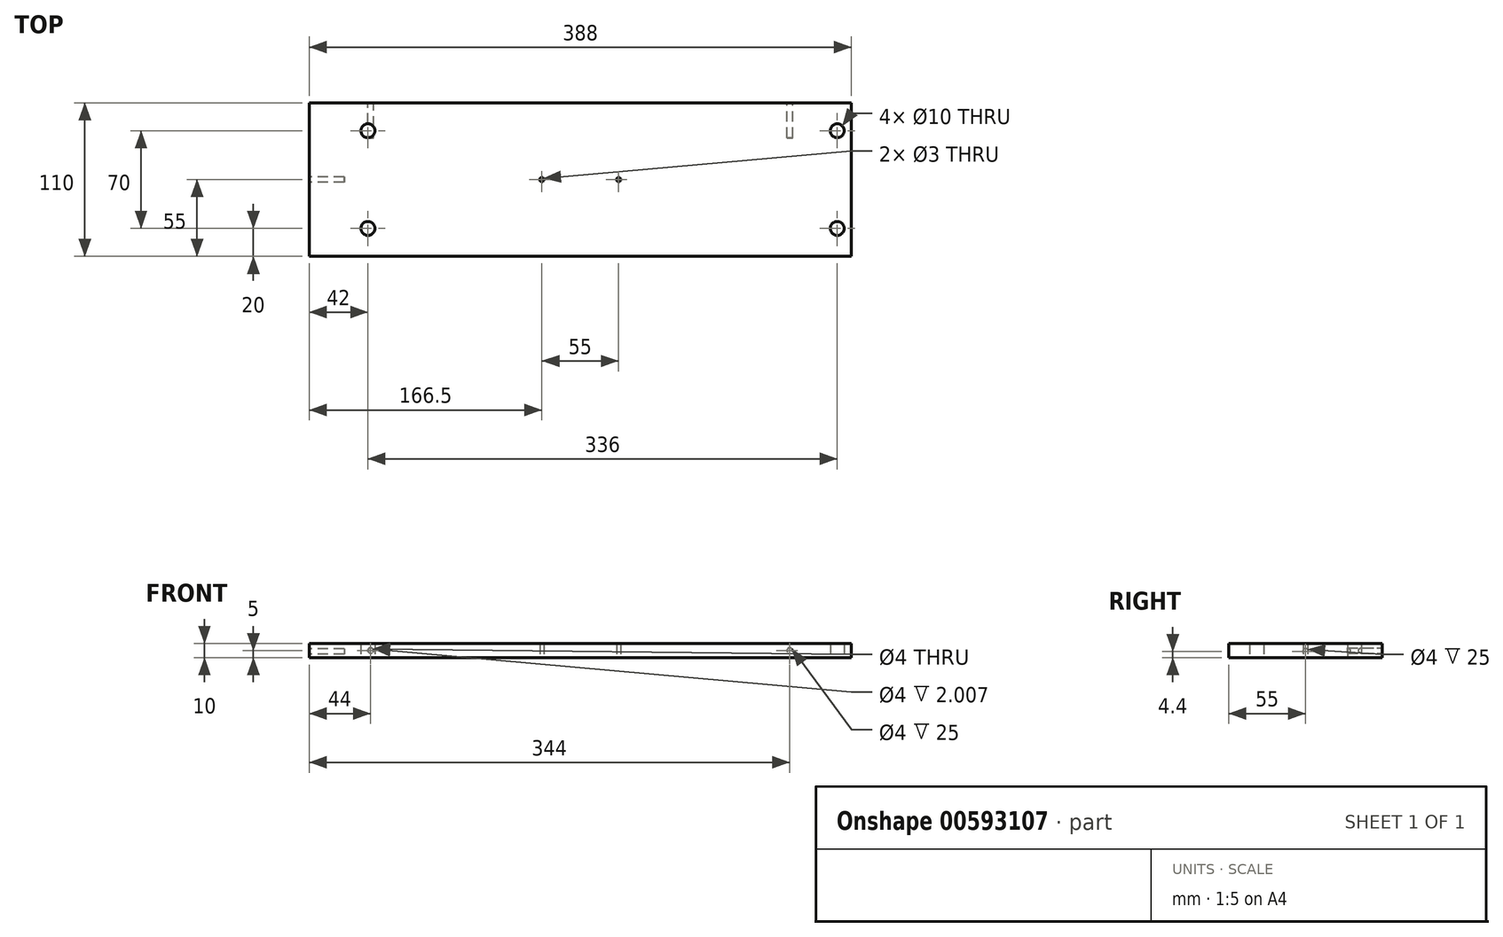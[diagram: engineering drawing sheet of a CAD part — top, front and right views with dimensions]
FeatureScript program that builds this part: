
annotation { "Feature Type Name" : "Feature", "Feature Type Description" : "" }
export const myFeature = defineFeature(function(context is Context, id is Id, definition is map)
    precondition{}
    {
        {
            var Q0;
            Q0=qCreatedBy(makeId("Top.planeOp"),FACE);
            var sketch = newSketch(context, id + "F0", { "sketchPlane" : qUnion([Q0])});
            skLineSegment(sketch, "E0.bottom", {"start": v(194, 55) * mm, "end": v(-194, 55) * mm});
            skLineSegment(sketch, "E0.top", {"start": v(194, -55) * mm, "end": v(-194, -55) * mm});
            skLineSegment(sketch, "E0.left", {"start": v(194, 55) * mm, "end": v(194, -55) * mm});
            skLineSegment(sketch, "E0.right", {"start": v(-194, 55) * mm, "end": v(-194, -55) * mm});
            skPoint(sketch, "E0.middle", {"position": v(0, 0) * mm});
            skCircle(sketch, "E1", {"center": v(184, 35) * mm, "radius": 5 * mm});
            skCircle(sketch, "E2", {"center": v(184, -35) * mm, "radius": 5 * mm});
            skLineSegment(sketch, "E3", {"start": v(184, 35) * mm, "end": v(184, -35) * mm, "construction": true});
            skPoint(sketch, "E4", {"position": v(184, 0) * mm});
            skCircle(sketch, "E5", {"center": v(-152, 35) * mm, "radius": 5 * mm});
            skCircle(sketch, "E6", {"center": v(-152, -35) * mm, "radius": 5 * mm});
            skLineSegment(sketch, "E7", {"start": v(-152, 35) * mm, "end": v(-152, -35) * mm, "construction": true});
            skPoint(sketch, "E8", {"position": v(-152, 0) * mm});
            skCircle(sketch, "E9", {"center": v(-27.5, 0) * mm, "radius": 1.5 * mm});
            skCircle(sketch, "E10", {"center": v(27.5, 0) * mm, "radius": 1.5 * mm});
            skLineSegment(sketch, "E11", {"start": v(-27.5, 0) * mm, "end": v(27.5, 0) * mm, "construction": true});
            skSolve(sketch);
        }
        {
            var Q0;
            Q0=makeQuery(id+"F0.imprint","IMPRINT",FACE,{"disambiguationData":[TD([[makeQuery(id+"F0.imprint","IMPRINT",EDGE,{"derivedFrom":sQuery(id+"F0.wireOp",EDGE,"E0.bottom")}),1.0]])]});
            extrude(context, id + "F1", {"entities" : qUnion([Q0]), "depth" : 10 * mm, "offsetDistance" : 25 * mm});
        }
        {
            var Q0;
            Q0=makeQuery(id+"F1.opExtrude","SWEPT_FACE",FACE,{"disambiguationData":[OSD([sQuery(id+"F0.wireOp",EDGE,"E0.right")])]});
            var sketch = newSketch(context, id + "F2", { "sketchPlane" : qUnion([Q0])});
            skCircle(sketch, "E12", {"center": v(0, 4.4) * mm, "radius": 2 * mm});
            skSolve(sketch);
        }
        {
            var Q0;
            Q0=qSketchRegion(id+"F2",true);
            extrude(context, id + "F3", {"entities" : qUnion([Q0]), "operationType" : NewBodyOperationType.REMOVE, "oppositeDirection" : true, "depth" : 25 * mm, "offsetDistance" : 25 * mm});
        }
        {
            var Q0;
            Q0=makeQuery(id+"F1.opExtrude","SWEPT_FACE",FACE,{"disambiguationData":[OSD([sQuery(id+"F0.wireOp",EDGE,"E0.bottom")])]});
            var sketch = newSketch(context, id + "F4", { "sketchPlane" : qUnion([Q0])});
            skCircle(sketch, "E13", {"center": v(-150, 5) * mm, "radius": 2 * mm});
            skCircle(sketch, "E14", {"center": v(150, 5) * mm, "radius": 2 * mm});
            skLineSegment(sketch, "E15", {"start": v(-150, 5) * mm, "end": v(150, 5) * mm, "construction": true});
            skPoint(sketch, "E16", {"position": v(0, 5) * mm});
            skSolve(sketch);
        }
        {
            var Q0;
            Q0=qSketchRegion(id+"F4",true);
            extrude(context, id + "F5", {"entities" : qUnion([Q0]), "operationType" : NewBodyOperationType.REMOVE, "oppositeDirection" : true, "depth" : 25 * mm, "offsetDistance" : 25 * mm});
        }
    });
